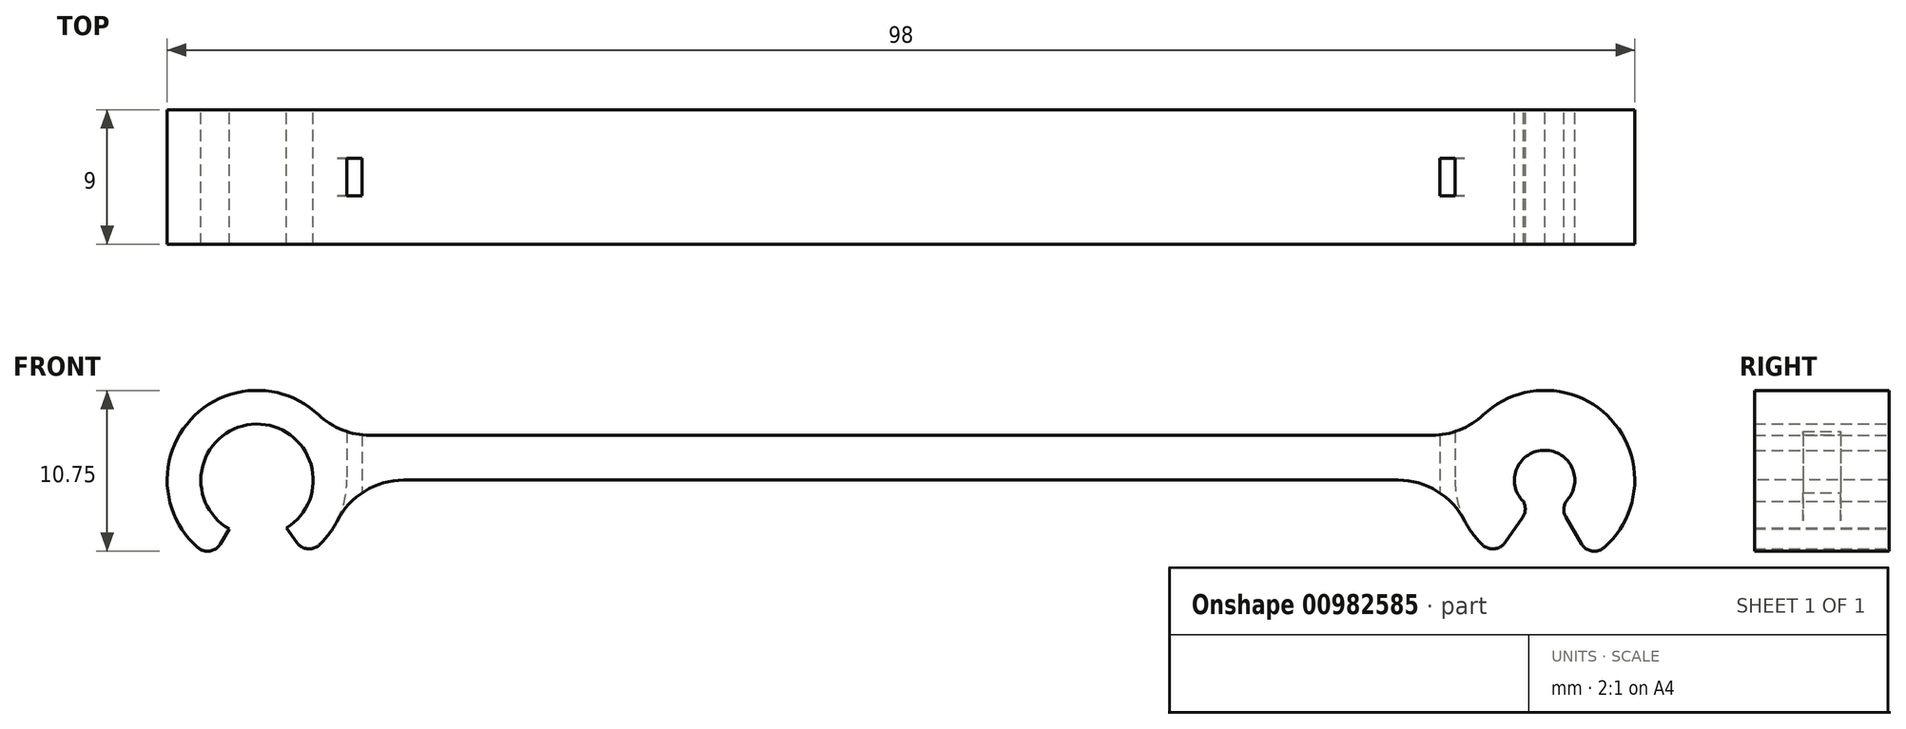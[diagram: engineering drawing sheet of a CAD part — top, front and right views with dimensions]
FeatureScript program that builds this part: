
annotation { "Feature Type Name" : "Feature", "Feature Type Description" : "" }
export const myFeature = defineFeature(function(context is Context, id is Id, definition is map)
    precondition{}
    {
        {
            var Q0;
            Q0=qCreatedBy(makeId("Front.planeOp"),FACE);
            var sketch = newSketch(context, id + "F0", { "sketchPlane" : qUnion([Q0])});
            skLineSegment(sketch, "E0", {"start": v(-43, 0) * mm, "end": v(43, 0) * mm});
            skCircle(sketch, "E1", {"center": v(-43, 0) * mm, "radius": 2 * mm});
            skCircle(sketch, "E2", {"center": v(-43, 0) * mm, "radius": 6 * mm});
            skLineSegment(sketch, "E3", {"start": v(-43.97, -1.75) * mm, "end": v(-46, -5.2) * mm});
            skLineSegment(sketch, "E4", {"start": v(-42.03, -1.75) * mm, "end": v(-39.74, -5.04) * mm});
            skLineSegment(sketch, "E5.MirrorCS", {"start": v(42.03, -1.75) * mm, "end": v(39.74, -5.04) * mm});
            skLineSegment(sketch, "E6.MirrorCS", {"start": v(43, 0) * mm, "end": v(-43, 0) * mm});
            skLineSegment(sketch, "E7.MirrorCS", {"start": v(43.97, -1.75) * mm, "end": v(46, -5.2) * mm});
            skCircle(sketch, "E8.MirrorC", {"center": v(43, 0) * mm, "radius": 2 * mm});
            skCircle(sketch, "E9.MirrorC", {"center": v(43, 0) * mm, "radius": 6 * mm});
            skSolve(sketch);
        }
        {
            var Q0;
            {var subQ0=sQuery(id+"F0.wireOp",EDGE,"E3");Q0=makeQuery(id+"F0.imprint","IMPRINT",FACE,{"disambiguationData":[TD([[makeQuery(id+"F0.imprint","IMPRINT",EDGE,{"derivedFrom":subQ0}),-1.0]])]});}
            var Q1;
            {var subQ0=sQuery(id+"F0.wireOp",EDGE,"E4");Q1=makeQuery(id+"F0.imprint","IMPRINT",FACE,{"disambiguationData":[TD([[makeQuery(id+"F0.imprint","IMPRINT",EDGE,{"derivedFrom":subQ0}),1.0]])]});}
            var Q2;
            {var subQ0=sQuery(id+"F0.wireOp",EDGE,"E5.MirrorCS");Q2=makeQuery(id+"F0.imprint","IMPRINT",FACE,{"disambiguationData":[TD([[makeQuery(id+"F0.imprint","IMPRINT",EDGE,{"derivedFrom":subQ0}),-1.0]])]});}
            var Q3;
            {var subQ5=sQuery(id+"F0.wireOp",EDGE,"E7.MirrorCS");Q3=makeQuery(id+"F0.imprint","IMPRINT",FACE,{"disambiguationData":[TD([[makeQuery(id+"F0.imprint","IMPRINT",EDGE,{"derivedFrom":subQ5}),1.0]])]});}
            extrude(context, id + "F1", {"entities" : qUnion([Q0, Q1, Q2, Q3]), "depth" : 9 * mm, "offsetDistance" : 25 * mm});
        }
        {
            var Q0;
            Q0=makeQuery(id+"F1.opExtrude","SWEPT_EDGE",EDGE,{"disambiguationData":[OSD([sQuery(id+"F0.wireOp",EDGE,"E5.MirrorCS"),sQuery(id+"F0.wireOp",EDGE,"E8.MirrorC")])]});
            var Q1;
            Q1=makeQuery(id+"F1.opExtrude","SWEPT_EDGE",EDGE,{"disambiguationData":[OSD([sQuery(id+"F0.wireOp",EDGE,"E7.MirrorCS"),sQuery(id+"F0.wireOp",EDGE,"E8.MirrorC")])]});
            var Q2;
            Q2=makeQuery(id+"F1.opExtrude","SWEPT_EDGE",EDGE,{"disambiguationData":[OSD([sQuery(id+"F0.wireOp",EDGE,"E1"),sQuery(id+"F0.wireOp",EDGE,"E4")])]});
            var Q3;
            Q3=makeQuery(id+"F1.opExtrude","SWEPT_EDGE",EDGE,{"disambiguationData":[OSD([sQuery(id+"F0.wireOp",EDGE,"E1"),sQuery(id+"F0.wireOp",EDGE,"E3")])]});
            var Q4;
            Q4=makeQuery(id+"F1.opExtrude","SWEPT_EDGE",EDGE,{"disambiguationData":[OSD([sQuery(id+"F0.wireOp",EDGE,"E2"),sQuery(id+"F0.wireOp",EDGE,"E4")])]});
            var Q5;
            Q5=makeQuery(id+"F1.opExtrude","SWEPT_EDGE",EDGE,{"disambiguationData":[OSD([sQuery(id+"F0.wireOp",EDGE,"E2"),sQuery(id+"F0.wireOp",EDGE,"E3")])]});
            var Q6;
            Q6=makeQuery(id+"F1.opExtrude","SWEPT_EDGE",EDGE,{"disambiguationData":[OSD([sQuery(id+"F0.wireOp",EDGE,"E5.MirrorCS"),sQuery(id+"F0.wireOp",EDGE,"E9.MirrorC")])]});
            var Q7;
            Q7=makeQuery(id+"F1.opExtrude","SWEPT_EDGE",EDGE,{"disambiguationData":[OSD([sQuery(id+"F0.wireOp",EDGE,"E7.MirrorCS"),sQuery(id+"F0.wireOp",EDGE,"E9.MirrorC")])]});
            fillet(context, id + "F2", {"entities" : qUnion([Q0, Q1, Q2, Q3, Q4, Q5, Q6, Q7]), "radius" : 1 * mm, "tangentPropagation" : true, "allowEdgeOverflow" : false});
        }
        {
            var Q0;
            Q0=qCreatedBy(makeId("Top.planeOp"),FACE);
            var sketch = newSketch(context, id + "F3", { "sketchPlane" : qUnion([Q0])});
            skLineSegment(sketch, "E10.bottom", {"start": v(-42.99, 0) * mm, "end": v(43.01, 0) * mm});
            skLineSegment(sketch, "E10.top", {"start": v(-42.99, -9) * mm, "end": v(43.01, -9) * mm});
            skLineSegment(sketch, "E10.left", {"start": v(-42.99, 0) * mm, "end": v(-42.99, -9) * mm});
            skLineSegment(sketch, "E10.right", {"start": v(43.01, 0) * mm, "end": v(43.01, -9) * mm});
            skSolve(sketch);
        }
        {
            var Q0;
            Q0=makeQuery(id+"F3.imprint","IMPRINT",FACE,{"disambiguationData":[TD([[makeQuery(id+"F3.imprint","IMPRINT",EDGE,{"derivedFrom":sQuery(id+"F3.wireOp",EDGE,"E10.bottom")}),-1.0]])]});
            extrude(context, id + "F4", {"entities" : qUnion([Q0]), "depth" : 3 * mm, "offsetDistance" : 25 * mm});
        }
        {
            var Q0;
            Q0=makeQuery(id+"F4.opExtrude","SWEPT_BODY",BODY,{"disambiguationData":[OSD([sQuery(id+"F3.wireOp",EDGE,"E10.bottom"),sQuery(id+"F3.wireOp",EDGE,"E10.top"),sQuery(id+"F3.wireOp",EDGE,"E10.left"),sQuery(id+"F3.wireOp",EDGE,"E10.right")])]});
            var Q1;
            Q1=makeQuery(id+"F1.opExtrude","SWEPT_BODY",BODY,{"disambiguationData":[OSD([sQuery(id+"F0.wireOp",EDGE,"E5.MirrorCS"),sQuery(id+"F0.wireOp",EDGE,"E7.MirrorCS"),sQuery(id+"F0.wireOp",EDGE,"E8.MirrorC"),sQuery(id+"F0.wireOp",EDGE,"E9.MirrorC")])]});
            booleanBodies(context, id + "F5", {"operationType" : BooleanOperationType.UNION, "tools" : qUnion([Q0, Q1])});
        }
        {
            var Q0;
            Q0=makeQuery(id+"F1.opExtrude","SWEPT_BODY",BODY,{"disambiguationData":[OSD([sQuery(id+"F0.wireOp",EDGE,"E1"),sQuery(id+"F0.wireOp",EDGE,"E2"),sQuery(id+"F0.wireOp",EDGE,"E3"),sQuery(id+"F0.wireOp",EDGE,"E4")])]});
            var Q1;
            Q1=makeQuery(id+"F4.opExtrude","SWEPT_BODY",BODY,{"disambiguationData":[OSD([sQuery(id+"F3.wireOp",EDGE,"E10.bottom"),sQuery(id+"F3.wireOp",EDGE,"E10.top"),sQuery(id+"F3.wireOp",EDGE,"E10.left"),sQuery(id+"F3.wireOp",EDGE,"E10.right")])]});
            booleanBodies(context, id + "F6", {"operationType" : BooleanOperationType.UNION, "tools" : qUnion([Q0, Q1])});
        }
        {
            var Q0;
            Q0=qCreatedBy(makeId("Front.planeOp"),FACE);
            var sketch = newSketch(context, id + "F7", { "sketchPlane" : qUnion([Q0])});
            skCircle(sketch, "E11", {"center": v(42.97, 0) * mm, "radius": 2 * mm});
            skCircle(sketch, "E12", {"center": v(-43, 0) * mm, "radius": 2 * mm});
            skSolve(sketch);
        }
        {
            var Q0;
            Q0=makeQuery(id+"F7.imprint","IMPRINT",FACE,{"disambiguationData":[TD([[makeQuery(id+"F7.imprint","IMPRINT",EDGE,{"derivedFrom":sQuery(id+"F7.wireOp",EDGE,"E12")}),1.0]])]});
            var Q1;
            Q1=makeQuery(id+"F7.imprint","IMPRINT",FACE,{"disambiguationData":[TD([[makeQuery(id+"F7.imprint","IMPRINT",EDGE,{"derivedFrom":sQuery(id+"F7.wireOp",EDGE,"E11")}),1.0]])]});
            extrude(context, id + "F8", {"entities" : qUnion([Q0, Q1]), "operationType" : NewBodyOperationType.REMOVE, "depth" : 25 * mm, "offsetDistance" : 25 * mm});
        }
        {
            var Q0;
            {var subQ0=sQuery(id+"F0.wireOp",EDGE,"E2");var subQ1=sQuery(id+"F0.wireOp",EDGE,"E9.MirrorC");var subQ10=sQuery(id+"F3.wireOp",EDGE,"E10.top");var subQ12=makeQuery(id+"F1.opExtrude","SWEPT_FACE",FACE,{"disambiguationData":[OSD([subQ1])]});var subQ13=sQuery(id+"F3.wireOp",EDGE,"E10.bottom");var subQ15=sQuery(id+"F3.wireOp",EDGE,"E10.left");Q0=makeQuery(id+"F6.opBoolean","SPLIT",FACE,{"disambiguationData":[TD([makeQuery(id+"F1.opExtrude","SWEPT_FACE",FACE,{"disambiguationData":[OSD([subQ0])]})])],"derivedFrom":makeQuery(id+"F5.opBoolean","SPLIT",FACE,{"disambiguationData":[TD([subQ12])],"derivedFrom":makeQuery(id+"F4.opExtrude","CAP_FACE",FACE,{"disambiguationData":[OSD([subQ13,subQ10,subQ15,sQuery(id+"F3.wireOp",EDGE,"E10.right")])],"isStart":true})})});}
            var sketch = newSketch(context, id + "F9", { "sketchPlane" : qUnion([Q0])});
            skLineSegment(sketch, "E13.bottom", {"start": v(37, 3.25) * mm, "end": v(36, 3.25) * mm});
            skLineSegment(sketch, "E13.top", {"start": v(37, 5.75) * mm, "end": v(36, 5.75) * mm});
            skLineSegment(sketch, "E13.left", {"start": v(37, 3.25) * mm, "end": v(37, 5.75) * mm});
            skLineSegment(sketch, "E13.right", {"start": v(36, 3.25) * mm, "end": v(36, 5.75) * mm});
            skLineSegment(sketch, "E14.MirrorCS", {"start": v(-37, 3.25) * mm, "end": v(-36, 3.25) * mm});
            skLineSegment(sketch, "E15.MirrorCS", {"start": v(-36, 3.25) * mm, "end": v(-36, 5.75) * mm});
            skLineSegment(sketch, "E16.MirrorCS", {"start": v(-37, 3.25) * mm, "end": v(-37, 5.75) * mm});
            skLineSegment(sketch, "E17.MirrorCS", {"start": v(-37, 5.75) * mm, "end": v(-36, 5.75) * mm});
            skSolve(sketch);
        }
        {
            var Q0;
            Q0=makeQuery(id+"F9.imprint","IMPRINT",FACE,{"disambiguationData":[TD([[makeQuery(id+"F9.imprint","IMPRINT",EDGE,{"derivedFrom":sQuery(id+"F9.wireOp",EDGE,"E13.bottom")}),-1.0]])]});
            var Q1;
            Q1=makeQuery(id+"F9.imprint","IMPRINT",FACE,{"disambiguationData":[TD([[makeQuery(id+"F9.imprint","IMPRINT",EDGE,{"derivedFrom":sQuery(id+"F9.wireOp",EDGE,"E14.MirrorCS")}),1.0]])]});
            var Q2;
            Q2=makeQuery(id+"F9.imprint","IMPRINT",FACE,{"disambiguationData":[TD([[makeQuery(id+"F9.imprint","IMPRINT",EDGE,{"derivedFrom":sQuery(id+"F9.wireOp",EDGE,"YbN0PLoJ-421t-fmgY-wpyC-S2v2ai4dtUob.bottom")}),-1.0]])]});
            var Q3;
            Q3=makeQuery(id+"F9.imprint","IMPRINT",FACE,{"disambiguationData":[TD([[makeQuery(id+"F9.imprint","IMPRINT",EDGE,{"derivedFrom":sQuery(id+"F9.wireOp",EDGE,"zw8rkDCZ-8q6K-Nz3p-cXrY-HS9gBNRIXkon.bottom")}),-1.0]])]});
            extrude(context, id + "F10", {"entities" : qUnion([Q0, Q1, Q2, Q3]), "operationType" : NewBodyOperationType.REMOVE, "oppositeDirection" : true, "depth" : 25 * mm, "offsetDistance" : 25 * mm});
        }
        {
            var Q0;
            Q0=qCreatedBy(makeId("Front.planeOp"),FACE);
            var sketch = newSketch(context, id + "F11", { "sketchPlane" : qUnion([Q0])});
            skLineSegment(sketch, "E18", {"start": v(0, 0) * mm, "end": v(-43, 0) * mm});
            skCircle(sketch, "E19", {"center": v(-43, 0) * mm, "radius": 3.75 * mm});
            skCircle(sketch, "E20.MirrorC", {"center": v(43, 0) * mm, "radius": 3.75 * mm});
            skSolve(sketch);
        }
        {
            var Q0;
            Q0=makeQuery(id+"F11.imprint","IMPRINT",FACE,{"disambiguationData":[TD([[makeQuery(id+"F11.imprint","IMPRINT",EDGE,{"derivedFrom":sQuery(id+"F11.wireOp",EDGE,"E19")}),1.0]])]});
            var Q1;
            Q1=makeQuery(id+"F11.imprint","IMPRINT",FACE,{"disambiguationData":[TD([[makeQuery(id+"F11.imprint","IMPRINT",EDGE,{"derivedFrom":sQuery(id+"F11.wireOp",EDGE,"E20.MirrorC")}),-1.0]])]});
            extrude(context, id + "F12", {"entities" : qUnion([Q0, Q1]), "operationType" : NewBodyOperationType.REMOVE, "depth" : 25 * mm, "offsetDistance" : 25 * mm});
        }
        {
            var Q0;
            Q0=makeQuery(id+"F5.opBoolean","INTERSECT",EDGE,{"derivedFrom":[makeQuery(id+"F1.opExtrude","SWEPT_FACE",FACE,{"disambiguationData":[OSD([sQuery(id+"F0.wireOp",EDGE,"E9.MirrorC")])]}),makeQuery(id+"F4.opExtrude","CAP_FACE",FACE,{"disambiguationData":[OSD([sQuery(id+"F3.wireOp",EDGE,"E10.bottom"),sQuery(id+"F3.wireOp",EDGE,"E10.top"),sQuery(id+"F3.wireOp",EDGE,"E10.left"),sQuery(id+"F3.wireOp",EDGE,"E10.right")])],"isStart":false})]});
            var Q1;
            Q1=makeQuery(id+"F6.opBoolean","INTERSECT",EDGE,{"derivedFrom":[makeQuery(id+"F1.opExtrude","SWEPT_FACE",FACE,{"disambiguationData":[OSD([sQuery(id+"F0.wireOp",EDGE,"E2")])]}),makeQuery(id+"F4.opExtrude","CAP_FACE",FACE,{"disambiguationData":[OSD([sQuery(id+"F3.wireOp",EDGE,"E10.bottom"),sQuery(id+"F3.wireOp",EDGE,"E10.top"),sQuery(id+"F3.wireOp",EDGE,"E10.left"),sQuery(id+"F3.wireOp",EDGE,"E10.right")])],"isStart":false})]});
            var Q2;
            {var subQ0=sQuery(id+"F3.wireOp",EDGE,"E10.left");var subQ1=sQuery(id+"F3.wireOp",EDGE,"E10.top");var subQ2=sQuery(id+"F3.wireOp",EDGE,"E10.bottom");var subQ3=makeQuery(id+"F4.opExtrude","CAP_FACE",FACE,{"disambiguationData":[OSD([subQ2,subQ1,subQ0,sQuery(id+"F3.wireOp",EDGE,"E10.right")])],"isStart":true});var subQ4=sQuery(id+"F0.wireOp",EDGE,"E9.MirrorC");var subQ9=makeQuery(id+"F4.opExtrude","SWEPT_FACE",FACE,{"disambiguationData":[OSD([subQ1])]});var subQ10=sQuery(id+"F0.wireOp",EDGE,"E2");var subQ11=makeQuery(id+"F1.opExtrude","SWEPT_FACE",FACE,{"disambiguationData":[OSD([subQ10])]});Q2=makeQuery(id+"F10.boolean.opBoolean","SPLIT",EDGE,{"disambiguationData":[TD([subQ9])],"derivedFrom":makeQuery(id+"F6.opBoolean","INTERSECT",EDGE,{"derivedFrom":[subQ11,makeQuery(id+"F5.opBoolean","SPLIT",FACE,{"disambiguationData":[TD([makeQuery(id+"F1.opExtrude","SWEPT_FACE",FACE,{"disambiguationData":[OSD([subQ4])]})])],"derivedFrom":subQ3})]})});}
            var Q3;
            {var subQ0=sQuery(id+"F3.wireOp",EDGE,"E10.top");var subQ1=makeQuery(id+"F4.opExtrude","CAP_FACE",FACE,{"disambiguationData":[OSD([sQuery(id+"F3.wireOp",EDGE,"E10.bottom"),subQ0,sQuery(id+"F3.wireOp",EDGE,"E10.left"),sQuery(id+"F3.wireOp",EDGE,"E10.right")])],"isStart":true});var subQ2=sQuery(id+"F0.wireOp",EDGE,"E9.MirrorC");var subQ3=makeQuery(id+"F1.opExtrude","SWEPT_FACE",FACE,{"disambiguationData":[OSD([subQ2])]});Q3=makeQuery(id+"F10.boolean.opBoolean","SPLIT",EDGE,{"disambiguationData":[TD([makeQuery(id+"F4.opExtrude","SWEPT_FACE",FACE,{"disambiguationData":[OSD([subQ0])]})])],"derivedFrom":makeQuery(id+"F5.opBoolean","INTERSECT",EDGE,{"derivedFrom":[subQ3,subQ1]})});}
            fillet(context, id + "F13", {"entities" : qUnion([Q0, Q1, Q2, Q3]), "radius" : 5 * mm, "tangentPropagation" : true, "allowEdgeOverflow" : false});
        }
    });
